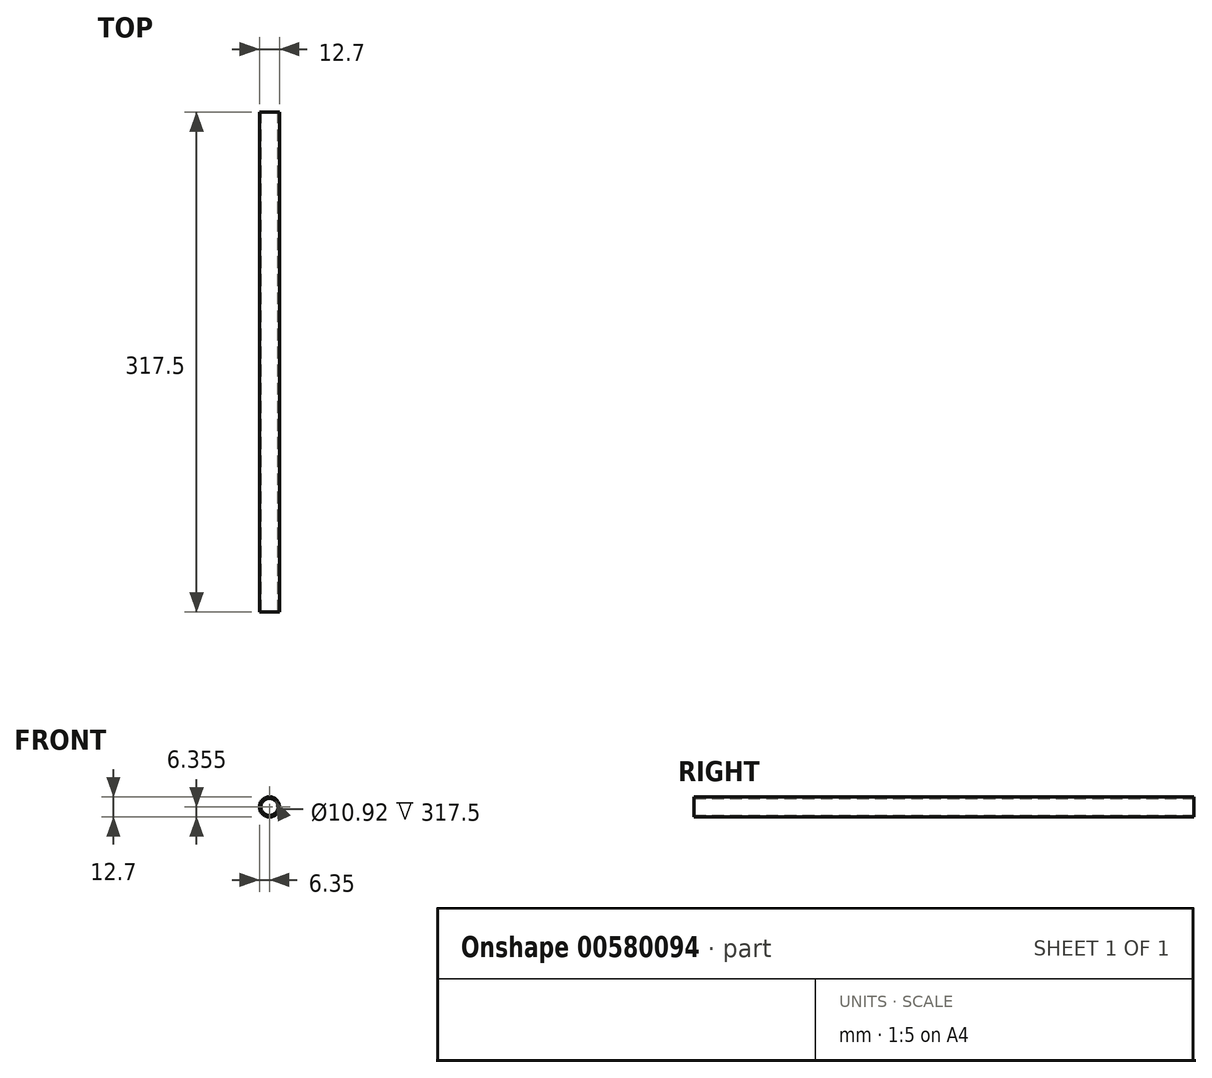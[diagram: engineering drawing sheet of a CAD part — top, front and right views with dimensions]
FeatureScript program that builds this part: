
annotation { "Feature Type Name" : "Feature", "Feature Type Description" : "" }
export const myFeature = defineFeature(function(context is Context, id is Id, definition is map)
    precondition{}
    {
        {
            var Q0;
            Q0=qCreatedBy(makeId("Front.planeOp"),FACE);
            var sketch = newSketch(context, id + "F0", { "sketchPlane" : qUnion([Q0])});
            skCircle(sketch, "E0", {"center": v(0, 1.31) * mm, "radius": 6.35 * mm});
            skSolve(sketch);
        }
        {
            var Q0;
            Q0=makeQuery(id+"F0.imprint","IMPRINT",FACE,{"disambiguationData":[TD([[makeQuery(id+"F0.imprint","IMPRINT",EDGE,{"derivedFrom":sQuery(id+"F0.wireOp",EDGE,"E0")}),1.0]])]});
            extrude(context, id + "F1", {"entities" : qUnion([Q0]), "depth" : 317.5 * mm, "offsetDistance" : 25.4 * mm, "symmetric" : true});
        }
        {
            var Q0;
            Q0=makeQuery(id+"F1.opExtrude","CAP_FACE",FACE,{"disambiguationData":[OSD([sQuery(id+"F0.wireOp",EDGE,"E0")])],"isStart":false});
            var Q1;
            Q1=makeQuery(id+"F1.opExtrude","CAP_FACE",FACE,{"disambiguationData":[OSD([sQuery(id+"F0.wireOp",EDGE,"E0")])],"isStart":true});
            shell(context, id + "F2", {"entities" : qUnion([Q0, Q1]), "thickness" : 0.89 * mm});
        }
    });
